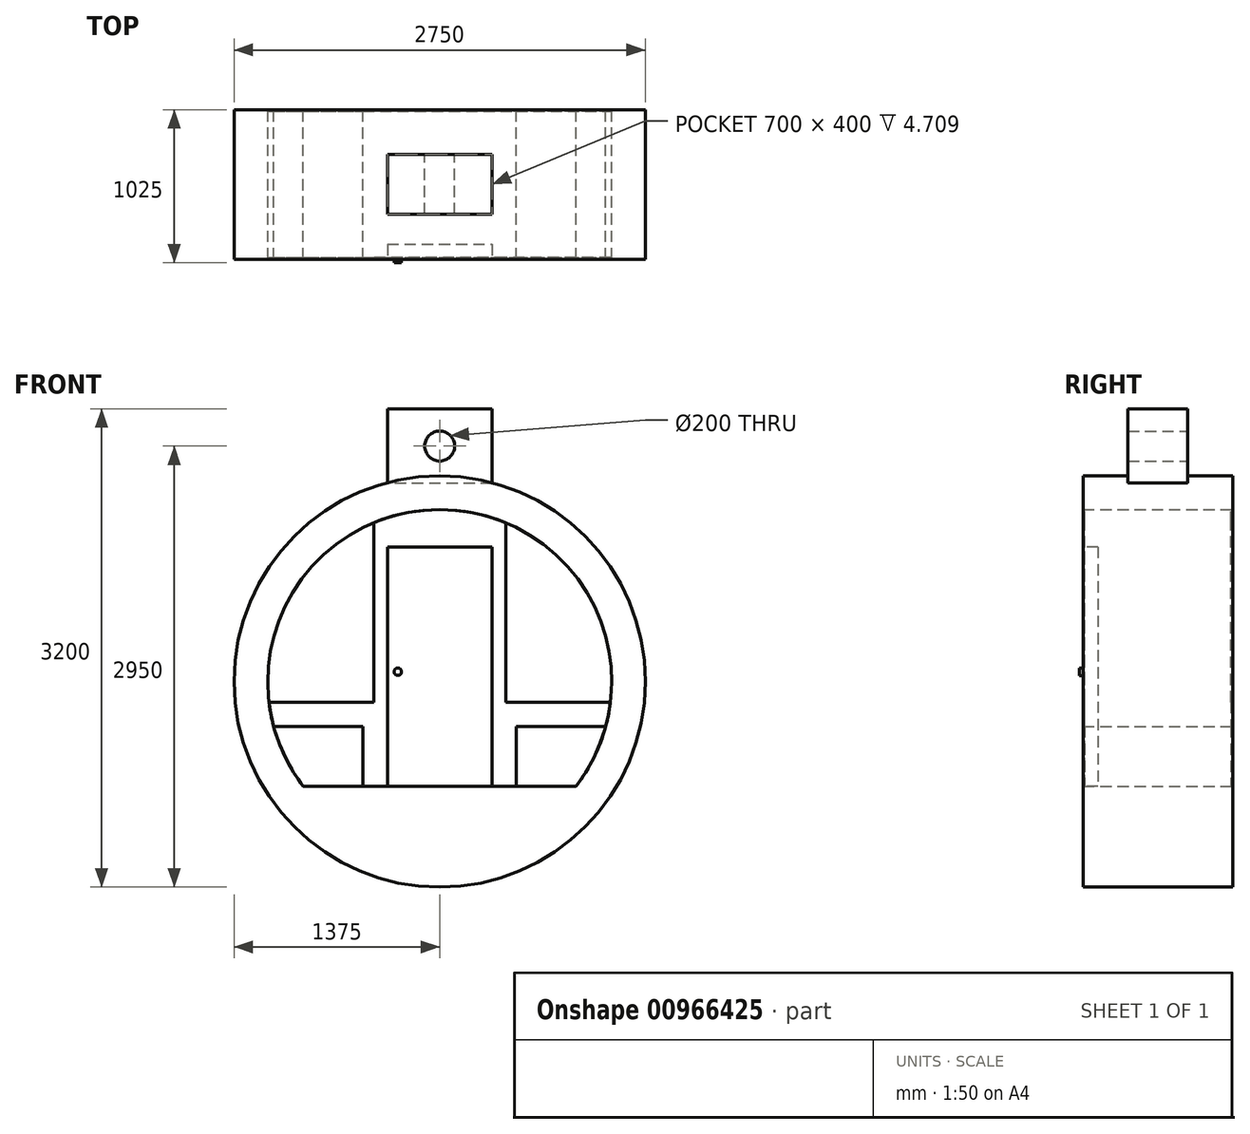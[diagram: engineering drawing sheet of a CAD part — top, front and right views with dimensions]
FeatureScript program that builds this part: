
annotation { "Feature Type Name" : "Feature", "Feature Type Description" : "" }
export const myFeature = defineFeature(function(context is Context, id is Id, definition is map)
    precondition{}
    {
        {
            var Q0;
            Q0=qCreatedBy(makeId("Front.planeOp"),FACE);
            var sketch = newSketch(context, id + "F0", { "sketchPlane" : qUnion([Q0])});
            skLineSegment(sketch, "E0.bottom", {"start": v(350, 3250) * mm, "end": v(-350, 3250) * mm});
            skLineSegment(sketch, "E0.top", {"start": v(350, 2750) * mm, "end": v(-350, 2750) * mm});
            skLineSegment(sketch, "E0.left", {"start": v(350, 3250) * mm, "end": v(350, 2750) * mm});
            skLineSegment(sketch, "E0.right", {"start": v(-350, 3250) * mm, "end": v(-350, 2750) * mm});
            skPoint(sketch, "E0.middle", {"position": v(0, 3000) * mm});
            skCircle(sketch, "E1", {"center": v(0, 3000) * mm, "radius": 100 * mm});
            skSolve(sketch);
        }
        {
            var Q0;
            Q0=qSketchRegion(id+"F0",true);
            extrude(context, id + "F1", {"entities" : qUnion([Q0]), "depth" : 400 * mm, "offsetDistance" : 25 * mm, "symmetric" : true});
        }
        {
            var Q0;
            Q0=qCreatedBy(makeId("Front.planeOp"),FACE);
            var sketch = newSketch(context, id + "F2", { "sketchPlane" : qUnion([Q0])});
            skLineSegment(sketch, "E2", {"start": v(0, 0) * mm, "end": v(0, 2750) * mm, "construction": true});
            skPoint(sketch, "E3", {"position": v(0, 1375) * mm});
            skCircle(sketch, "E4", {"center": v(0, 1375) * mm, "radius": 1375 * mm});
            skCircle(sketch, "E5", {"center": v(0, 1375) * mm, "radius": 1150 * mm});
            skLineSegment(sketch, "E6", {"start": v(-912.41, 675) * mm, "end": v(912.41, 675) * mm});
            skSolve(sketch);
        }
        {
            var Q0;
            Q0=qSketchRegion(id+"F2",true);
            var Q1;
            {var subQ0=sQuery(id+"F2.wireOp",EDGE,"E6");Q1=makeQuery(id+"F2.imprint","IMPRINT",FACE,{"disambiguationData":[TD([[makeQuery(id+"F2.imprint","IMPRINT",EDGE,{"derivedFrom":subQ0}),-1.0]])]});}
            extrude(context, id + "F3", {"entities" : qUnion([Q0, Q1]), "operationType" : NewBodyOperationType.ADD, "depth" : 1000 * mm, "offsetDistance" : 25 * mm, "symmetric" : true});
        }
        {
            var Q0;
            Q0=qCreatedBy(makeId("Front.planeOp"),FACE);
            var sketch = newSketch(context, id + "F4", { "sketchPlane" : qUnion([Q0])});
            skLineSegment(sketch, "E7", {"start": v(512.41, 675) * mm, "end": v(512.41, 1075) * mm});
            skLineSegment(sketch, "E8", {"start": v(512.41, 1075) * mm, "end": v(1110.18, 1075) * mm});
            skLineSegment(sketch, "E9.MirrorCS", {"start": v(-512.41, 675) * mm, "end": v(-512.41, 1075) * mm});
            skLineSegment(sketch, "E10.MirrorCS", {"start": v(-512.41, 1075) * mm, "end": v(-1110.18, 1075) * mm});
            skLineSegment(sketch, "E11", {"start": v(512.41, 675) * mm, "end": v(912.41, 675) * mm});
            skArc(sketch, "E12", {"start": v(912.41, 675) * mm, "mid": v(1030.88, 865.32) * mm, "end": v(1110.18, 1075) * mm});
            skArc(sketch, "E13.MirrorCS", {"start": v(-912.41, 675) * mm, "mid": v(-1030.88, 865.32) * mm, "end": v(-1110.18, 1075) * mm});
            skLineSegment(sketch, "E14.MirrorCS", {"start": v(-512.41, 675) * mm, "end": v(-912.41, 675) * mm});
            skSolve(sketch);
        }
        {
            var Q0;
            Q0=qSketchRegion(id+"F4",true);
            extrude(context, id + "F5", {"entities" : qUnion([Q0]), "depth" : 1000 * mm, "offsetDistance" : 25 * mm, "symmetric" : true});
        }
        {
            var Q0;
            Q0=makeQuery(id+"F3.opExtrude","CAP_FACE",FACE,{"disambiguationData":[OSD([sQuery(id+"F2.wireOp",EDGE,"E4"),sQuery(id+"F2.wireOp",EDGE,"E5"),sQuery(id+"F2.wireOp",EDGE,"E6")])],"isStart":false});
            var sketch = newSketch(context, id + "F6", { "sketchPlane" : qUnion([Q0])});
            skLineSegment(sketch, "E15", {"start": v(-350, 2275) * mm, "end": v(350, 2275) * mm});
            skLineSegment(sketch, "E16", {"start": v(350, 2275) * mm, "end": v(350, 675) * mm});
            skLineSegment(sketch, "E17", {"start": v(350, 675) * mm, "end": v(-350, 675) * mm});
            skLineSegment(sketch, "E18", {"start": v(-350, 675) * mm, "end": v(-350, 2275) * mm});
            skPoint(sketch, "E19", {"position": v(0, 675) * mm});
            skSolve(sketch);
        }
        {
            var Q0;
            Q0=qSketchRegion(id+"F6",true);
            extrude(context, id + "F7", {"entities" : qUnion([Q0]), "oppositeDirection" : true, "depth" : 100 * mm, "offsetDistance" : 25 * mm});
        }
        {
            var Q0;
            Q0=makeQuery(id+"F7.opExtrude","CAP_FACE",FACE,{"disambiguationData":[OSD([sQuery(id+"F6.wireOp",EDGE,"E15"),sQuery(id+"F6.wireOp",EDGE,"E16"),sQuery(id+"F6.wireOp",EDGE,"E17"),sQuery(id+"F6.wireOp",EDGE,"E18")])],"isStart":true});
            var sketch = newSketch(context, id + "F8", { "sketchPlane" : qUnion([Q0])});
            skCircle(sketch, "E20", {"center": v(-280, 1440.53) * mm, "radius": 25 * mm});
            skSolve(sketch);
        }
        {
            var Q0;
            Q0=qSketchRegion(id+"F8",true);
            extrude(context, id + "F9", {"entities" : qUnion([Q0]), "depth" : 25 * mm, "offsetDistance" : 25 * mm});
        }
        {
            var Q0;
            Q0=makeQuery(id+"F7.opExtrude","CAP_FACE",FACE,{"disambiguationData":[OSD([sQuery(id+"F6.wireOp",EDGE,"E15"),sQuery(id+"F6.wireOp",EDGE,"E16"),sQuery(id+"F6.wireOp",EDGE,"E17"),sQuery(id+"F6.wireOp",EDGE,"E18")])],"isStart":true});
            var sketch = newSketch(context, id + "F10", { "sketchPlane" : qUnion([Q0])});
            skLineSegment(sketch, "E21", {"start": v(-1141.67, 1236.8) * mm, "end": v(-441.67, 1236.8) * mm});
            skLineSegment(sketch, "E22", {"start": v(-441.67, 1236.8) * mm, "end": v(-441.67, 2436.8) * mm});
            skArc(sketch, "E23", {"start": v(-441.67, 2436.8) * mm, "mid": v(0, 2525) * mm, "end": v(441.67, 2436.8) * mm});
            skArc(sketch, "E24", {"start": v(-1141.67, 1236.8) * mm, "mid": v(-1128.83, 1155.34) * mm, "end": v(-1110.18, 1075) * mm});
            skLineSegment(sketch, "E25.MirrorCS", {"start": v(441.67, 1236.8) * mm, "end": v(441.67, 2436.8) * mm});
            skLineSegment(sketch, "E26.MirrorCS", {"start": v(1141.67, 1236.8) * mm, "end": v(441.67, 1236.8) * mm});
            skArc(sketch, "E27.MirrorCS", {"start": v(1141.67, 1236.8) * mm, "mid": v(1128.83, 1155.34) * mm, "end": v(1110.18, 1075) * mm});
            skLineSegment(sketch, "E28", {"start": v(-1110.18, 1075) * mm, "end": v(-512.41, 1075) * mm});
            skLineSegment(sketch, "E29", {"start": v(-512.41, 1075) * mm, "end": v(-512.41, 675) * mm});
            skLineSegment(sketch, "E30", {"start": v(-512.41, 675) * mm, "end": v(-350, 675) * mm});
            skLineSegment(sketch, "E31", {"start": v(-350, 675) * mm, "end": v(-350, 2275) * mm});
            skLineSegment(sketch, "E32", {"start": v(-350, 2275) * mm, "end": v(350, 2275) * mm});
            skLineSegment(sketch, "E33", {"start": v(350, 2275) * mm, "end": v(350, 675) * mm});
            skLineSegment(sketch, "E34", {"start": v(350, 675) * mm, "end": v(512.41, 675) * mm});
            skLineSegment(sketch, "E35", {"start": v(512.41, 675) * mm, "end": v(512.41, 1075) * mm});
            skLineSegment(sketch, "E36", {"start": v(512.41, 1075) * mm, "end": v(1110.18, 1075) * mm});
            skSolve(sketch);
        }
        {
            var Q0;
            Q0=qSketchRegion(id+"F10",true);
            extrude(context, id + "F11", {"entities" : qUnion([Q0]), "oppositeDirection" : true, "depth" : 10 * mm, "offsetDistance" : 25 * mm});
        }
        {
            var Q0;
            Q0=makeQuery(id+"F11.opExtrude","SWEPT_BODY",BODY,{"disambiguationData":[OSD([sQuery(id+"F10.wireOp",EDGE,"E21"),sQuery(id+"F10.wireOp",EDGE,"E22"),sQuery(id+"F10.wireOp",EDGE,"E23"),sQuery(id+"F10.wireOp",EDGE,"E24"),sQuery(id+"F10.wireOp",EDGE,"E25.MirrorCS"),sQuery(id+"F10.wireOp",EDGE,"E26.MirrorCS"),sQuery(id+"F10.wireOp",EDGE,"E27.MirrorCS"),sQuery(id+"F10.wireOp",EDGE,"E28"),sQuery(id+"F10.wireOp",EDGE,"E29"),sQuery(id+"F10.wireOp",EDGE,"E30"),sQuery(id+"F10.wireOp",EDGE,"E31"),sQuery(id+"F10.wireOp",EDGE,"E32"),sQuery(id+"F10.wireOp",EDGE,"E33"),sQuery(id+"F10.wireOp",EDGE,"E34"),sQuery(id+"F10.wireOp",EDGE,"E35"),sQuery(id+"F10.wireOp",EDGE,"E36")])]});
            var Q1;
            Q1=qCreatedBy(makeId("Front.planeOp"),FACE);
            mirror(context, id + "F12", {"entities" : qUnion([Q0]), "mirrorPlane" : qUnion([Q1])});
        }
        {
            var Q0;
            Q0=makeQuery(id+"F12.opPattern","COPY",FACE,{"derivedFrom":makeQuery(id+"F11.opExtrude","CAP_FACE",FACE,{"disambiguationData":[OSD([sQuery(id+"F10.wireOp",EDGE,"E21"),sQuery(id+"F10.wireOp",EDGE,"E22"),sQuery(id+"F10.wireOp",EDGE,"E23"),sQuery(id+"F10.wireOp",EDGE,"E24"),sQuery(id+"F10.wireOp",EDGE,"E25.MirrorCS"),sQuery(id+"F10.wireOp",EDGE,"E26.MirrorCS"),sQuery(id+"F10.wireOp",EDGE,"E27.MirrorCS"),sQuery(id+"F10.wireOp",EDGE,"E28"),sQuery(id+"F10.wireOp",EDGE,"E29"),sQuery(id+"F10.wireOp",EDGE,"E30"),sQuery(id+"F10.wireOp",EDGE,"E31"),sQuery(id+"F10.wireOp",EDGE,"E32"),sQuery(id+"F10.wireOp",EDGE,"E33"),sQuery(id+"F10.wireOp",EDGE,"E34"),sQuery(id+"F10.wireOp",EDGE,"E35"),sQuery(id+"F10.wireOp",EDGE,"E36")])],"isStart":true}),"instanceName":"1"});
            var sketch = newSketch(context, id + "F13", { "sketchPlane" : qUnion([Q0])});
            skLineSegment(sketch, "E37.bottom", {"start": v(-350, 2275) * mm, "end": v(350, 2275) * mm});
            skLineSegment(sketch, "E37.top", {"start": v(-350, 675) * mm, "end": v(350, 675) * mm});
            skLineSegment(sketch, "E37.left", {"start": v(-350, 2275) * mm, "end": v(-350, 675) * mm});
            skLineSegment(sketch, "E37.right", {"start": v(350, 2275) * mm, "end": v(350, 675) * mm});
            skSolve(sketch);
        }
        {
            var Q0;
            Q0=qSketchRegion(id+"F13",true);
            extrude(context, id + "F14", {"entities" : qUnion([Q0]), "operationType" : NewBodyOperationType.ADD, "oppositeDirection" : true, "depth" : 10 * mm, "offsetDistance" : 25 * mm});
        }
        {
            var Q0;
            Q0=makeQuery(id+"F1.opExtrude","SWEPT_BODY",BODY,{"disambiguationData":[OSD([sQuery(id+"F0.wireOp",EDGE,"E0.bottom"),sQuery(id+"F0.wireOp",EDGE,"E0.top"),sQuery(id+"F0.wireOp",EDGE,"E0.left"),sQuery(id+"F0.wireOp",EDGE,"E0.right"),sQuery(id+"F0.wireOp",EDGE,"E1")])]});
            transform(context, id + "F15", {"entities" : qUnion([Q0]), "transformType" : TransformType.TRANSLATION_3D, "dx" : 0 * mm, "dy" : 0 * mm, "dz" : -50 * mm, "makeCopy" : false});
        }
        {
            var Q0;
            Q0=makeQuery(id+"F1.opExtrude","SWEPT_BODY",BODY,{"disambiguationData":[OSD([sQuery(id+"F0.wireOp",EDGE,"E0.bottom"),sQuery(id+"F0.wireOp",EDGE,"E0.top"),sQuery(id+"F0.wireOp",EDGE,"E0.left"),sQuery(id+"F0.wireOp",EDGE,"E0.right"),sQuery(id+"F0.wireOp",EDGE,"E1")])]});
            var Q1;
            Q1=makeQuery(id+"F3.opExtrude","SWEPT_BODY",BODY,{"disambiguationData":[OSD([sQuery(id+"F2.wireOp",EDGE,"E4"),sQuery(id+"F2.wireOp",EDGE,"E5"),sQuery(id+"F2.wireOp",EDGE,"E6")])]});
            booleanBodies(context, id + "F16", {"operationType" : BooleanOperationType.SUBTRACTION, "tools" : qUnion([Q0]), "targets" : qUnion([Q1]), "keepTools" : true});
        }
    });
